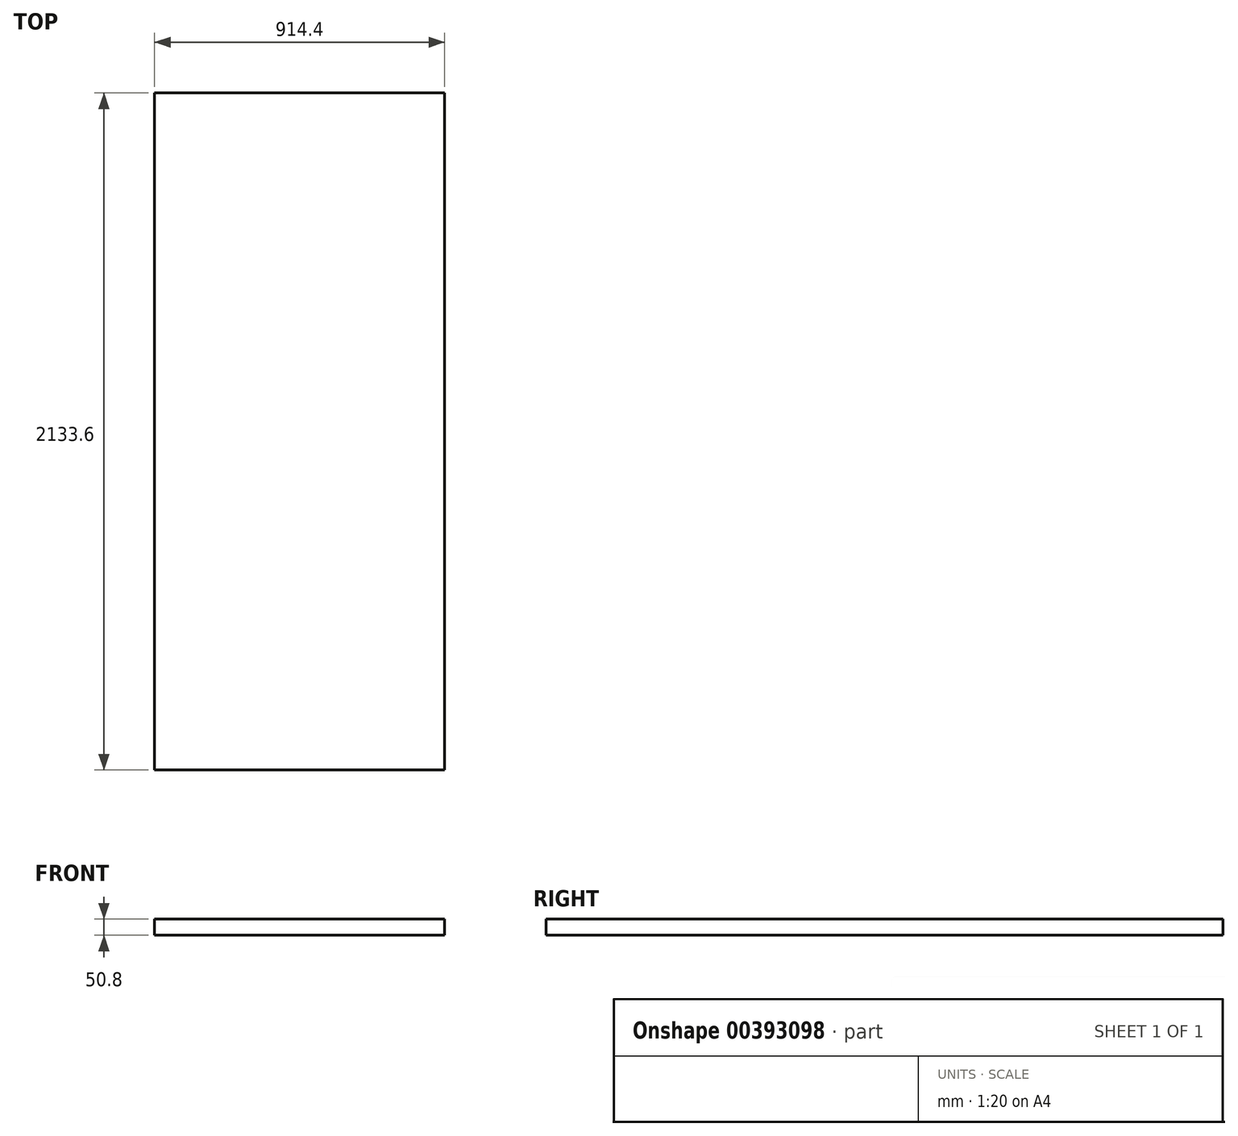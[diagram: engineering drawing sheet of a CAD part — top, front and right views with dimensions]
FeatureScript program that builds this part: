
annotation { "Feature Type Name" : "Feature", "Feature Type Description" : "" }
export const myFeature = defineFeature(function(context is Context, id is Id, definition is map)
    precondition{}
    {
        {
            var Q0;
            Q0=qCreatedBy(makeId("Front.planeOp"),FACE);
            var sketch = newSketch(context, id + "F0", { "sketchPlane" : qUnion([Q0])});
            skLineSegment(sketch, "E0.bottom", {"start": v(-457.2, 25.4) * mm, "end": v(457.2, 25.4) * mm});
            skLineSegment(sketch, "E0.top", {"start": v(-457.2, -25.4) * mm, "end": v(457.2, -25.4) * mm});
            skLineSegment(sketch, "E0.left", {"start": v(-457.2, 25.4) * mm, "end": v(-457.2, -25.4) * mm});
            skLineSegment(sketch, "E0.right", {"start": v(457.2, 25.4) * mm, "end": v(457.2, -25.4) * mm});
            skPoint(sketch, "E0.middle", {"position": v(0, 0) * mm});
            skSolve(sketch);
        }
        {
            var Q0;
            Q0 = qSketchRegion(id + "F0", true);
            extrude(context, id + "F1", {"entities" : qUnion([Q0]), "endBound" : BoundingType.SYMMETRIC, "depth" : 7 * 304.8 * mm});
        }
    });
